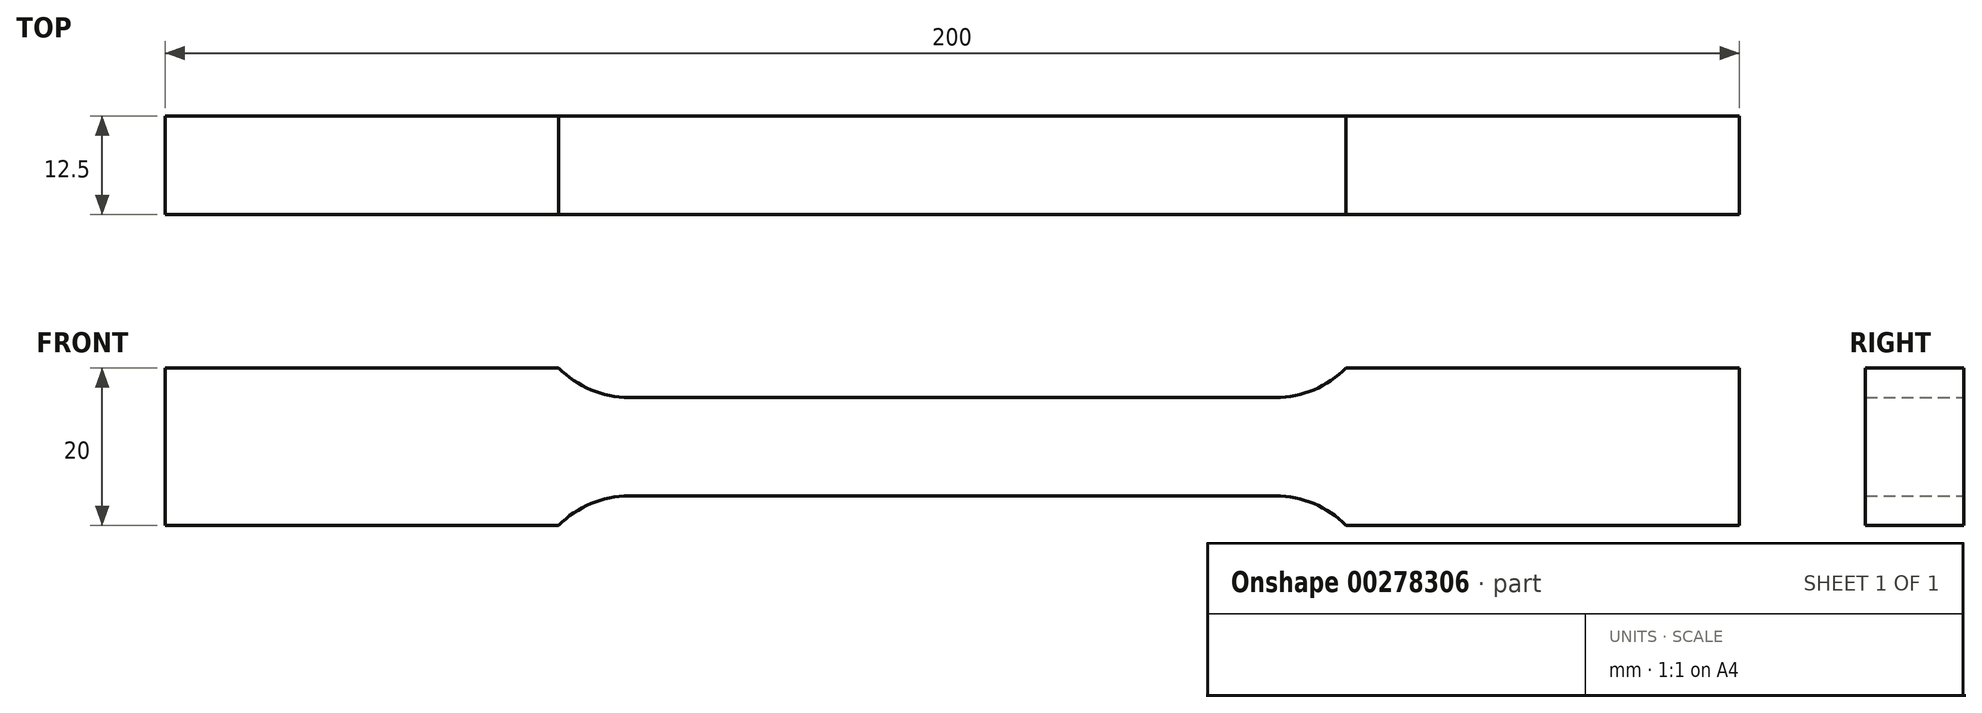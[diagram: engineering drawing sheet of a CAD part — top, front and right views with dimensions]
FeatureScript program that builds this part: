
annotation { "Feature Type Name" : "Feature", "Feature Type Description" : "" }
export const myFeature = defineFeature(function(context is Context, id is Id, definition is map)
    precondition{}
    {
        {
            var Q0;
            Q0=qCreatedBy(makeId("Front.planeOp"),FACE);
            var sketch = newSketch(context, id + "F0", { "sketchPlane" : qUnion([Q0])});
            skLineSegment(sketch, "E0", {"start": v(0, 6.25) * mm, "end": v(41.07, 6.25) * mm});
            skArc(sketch, "E1", {"start": v(41.07, 6.25) * mm, "mid": v(45.92, 7.23) * mm, "end": v(50, 10) * mm});
            skLineSegment(sketch, "E2", {"start": v(50, 10) * mm, "end": v(100, 10) * mm});
            skLineSegment(sketch, "E3", {"start": v(100, 10) * mm, "end": v(100, 0) * mm});
            skLineSegment(sketch, "E4.MirrorCS", {"start": v(50, -10) * mm, "end": v(100, -10) * mm});
            skLineSegment(sketch, "E5.MirrorCS", {"start": v(100, -10) * mm, "end": v(100, 0) * mm});
            skLineSegment(sketch, "E6.MirrorCS", {"start": v(0, -6.25) * mm, "end": v(41.07, -6.25) * mm});
            skArc(sketch, "E7.MirrorCS", {"start": v(41.07, -6.25) * mm, "mid": v(45.92, -7.23) * mm, "end": v(50, -10) * mm});
            skLineSegment(sketch, "E8.MirrorCS", {"start": v(-50, 10) * mm, "end": v(-100, 10) * mm});
            skLineSegment(sketch, "E9.MirrorCS", {"start": v(-50, -10) * mm, "end": v(-100, -10) * mm});
            skArc(sketch, "E10.MirrorCS", {"start": v(-41.07, -6.25) * mm, "mid": v(-45.92, -7.23) * mm, "end": v(-50, -10) * mm});
            skLineSegment(sketch, "E11.MirrorCS", {"start": v(0, -6.25) * mm, "end": v(-41.07, -6.25) * mm});
            skArc(sketch, "E12.MirrorCS", {"start": v(-41.07, 6.25) * mm, "mid": v(-45.92, 7.23) * mm, "end": v(-50, 10) * mm});
            skLineSegment(sketch, "E13.MirrorCS", {"start": v(-100, -10) * mm, "end": v(-100, 0) * mm});
            skLineSegment(sketch, "E14.MirrorCS", {"start": v(-100, 10) * mm, "end": v(-100, 0) * mm});
            skLineSegment(sketch, "E15.MirrorCS", {"start": v(0, 6.25) * mm, "end": v(-41.07, 6.25) * mm});
            skSolve(sketch);
        }
        {
            var Q0;
            Q0 = qSketchRegion(id + "F0", true);
            extrude(context, id + "F1", {"entities" : qUnion([Q0]), "endBound" : BoundingType.SYMMETRIC, "depth" : 12.5 * mm});
        }
    });
